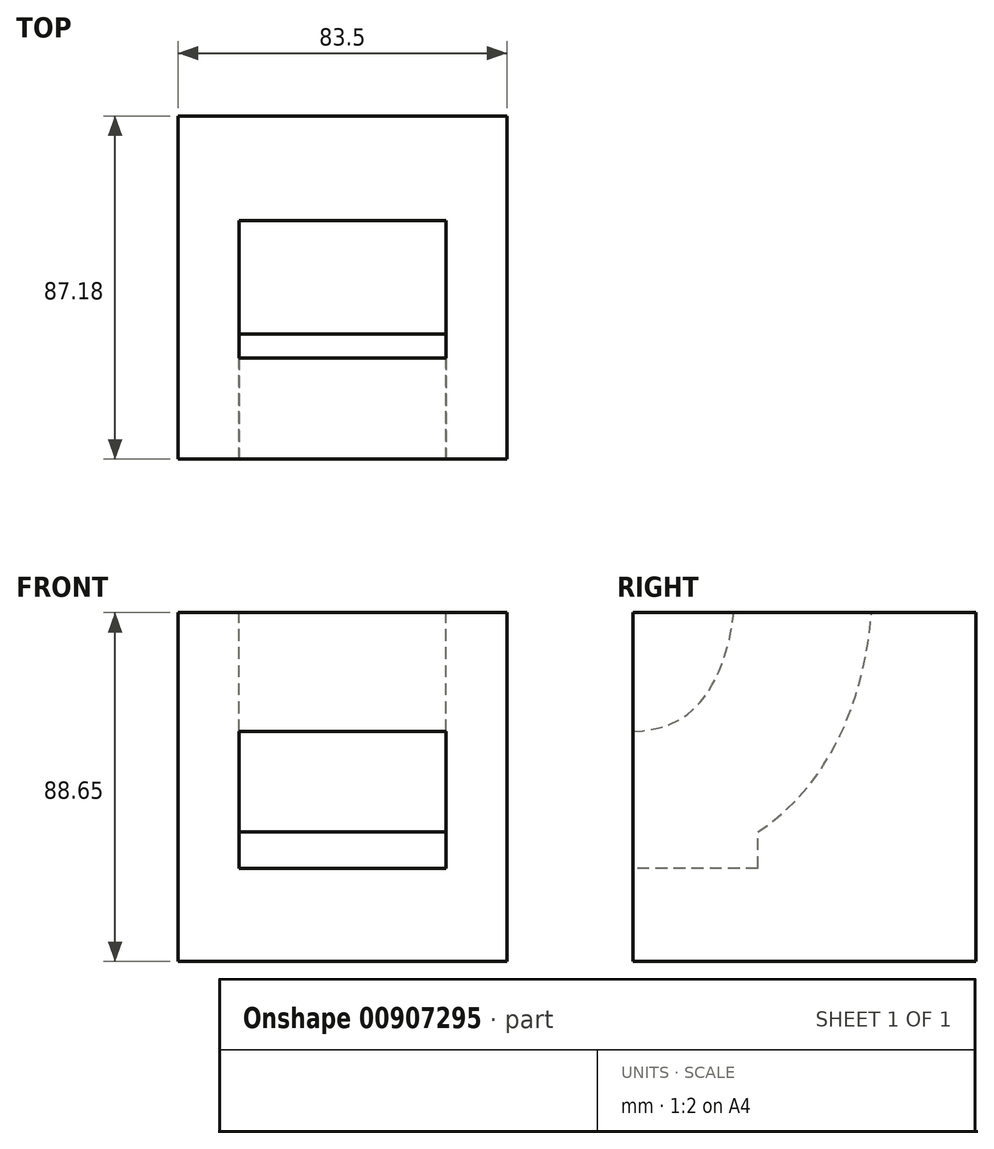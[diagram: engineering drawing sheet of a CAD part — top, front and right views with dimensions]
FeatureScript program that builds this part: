
annotation { "Feature Type Name" : "Feature", "Feature Type Description" : "" }
export const myFeature = defineFeature(function(context is Context, id is Id, definition is map)
    precondition{}
    {
        {
            var Q0;
            Q0=qCreatedBy(makeId("Top.planeOp"),FACE);
            var sketch = newSketch(context, id + "F0", { "sketchPlane" : qUnion([Q0])});
            skLineSegment(sketch, "E0.bottom", {"start": v(41.75, -43.6) * mm, "end": v(-41.75, -43.6) * mm});
            skLineSegment(sketch, "E0.top", {"start": v(41.75, 43.6) * mm, "end": v(-41.75, 43.6) * mm});
            skLineSegment(sketch, "E0.left", {"start": v(41.75, -43.6) * mm, "end": v(41.75, 43.6) * mm});
            skLineSegment(sketch, "E0.right", {"start": v(-41.75, -43.6) * mm, "end": v(-41.75, 43.6) * mm});
            skPoint(sketch, "E0.middle", {"position": v(0, 0) * mm});
            skSolve(sketch);
        }
        {
            var Q0;
            Q0 = qSketchRegion(id + "F0", true);
            extrude(context, id + "F1", {"entities" : qUnion([Q0]), "depth" : 88.65 * mm, "offsetDistance" : 25.4 * mm});
        }
        {
            var Q0;
            Q0=makeQuery(id+"F1.opExtrude","SWEPT_FACE",FACE,{"disambiguationData":[OSD([sQuery(id+"F0.wireOp",EDGE,"E0.bottom")])]});
            var sketch = newSketch(context, id + "F2", { "sketchPlane" : qUnion([Q0])});
            skLineSegment(sketch, "E1.bottom", {"start": v(26.3, 23.7) * mm, "end": v(-26.3, 23.7) * mm});
            skLineSegment(sketch, "E1.top", {"start": v(26.3, 58.47) * mm, "end": v(-26.3, 58.47) * mm});
            skLineSegment(sketch, "E1.left", {"start": v(26.3, 23.7) * mm, "end": v(26.3, 58.47) * mm});
            skLineSegment(sketch, "E1.right", {"start": v(-26.3, 23.7) * mm, "end": v(-26.3, 58.47) * mm});
            skPoint(sketch, "E1.middle", {"position": v(0, 41.09) * mm});
            skSolve(sketch);
        }
        {
            var Q0;
            Q0=qCreatedBy(makeId("Right.planeOp"),FACE);
            var sketch = newSketch(context, id + "F3", { "sketchPlane" : qUnion([Q0])});
            skFitSpline(sketch, "E2", {"points": [v(-43.6, 41.09) * mm, v(0, 97.57) * mm], "startDerivative": vector(99.1, 1.86) * mm, "endDerivative": vector(0, 77.57) * mm});
            skSolve(sketch);
        }
        {
            var Q0;
            Q0=makeQuery(id+"F2.imprint","IMPRINT",FACE,{"disambiguationData":[TD([[makeQuery(id+"F2.imprint","IMPRINT",EDGE,{"derivedFrom":sQuery(id+"F2.wireOp",EDGE,"E1.bottom")}),-1.0]])]});
            var Q1;
            Q1=sQuery(id+"F3.wireOp",EDGE,"E2");
            sweep(context, id + "F4", {"operationType" : NewBodyOperationType.REMOVE, "profiles" : qUnion([Q0]), "path" : qUnion([Q1])});
        }
        {
            var Q0;
            Q0 = qSketchRegion(id + "F2", true);
            extrude(context, id + "F5", {"entities" : qUnion([Q0]), "operationType" : NewBodyOperationType.REMOVE, "oppositeDirection" : true, "depth" : 31.75 * mm, "offsetDistance" : 25.4 * mm});
        }
    });
